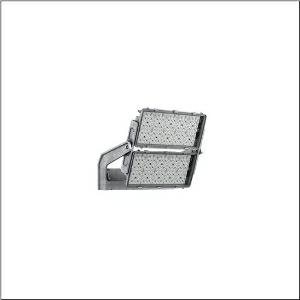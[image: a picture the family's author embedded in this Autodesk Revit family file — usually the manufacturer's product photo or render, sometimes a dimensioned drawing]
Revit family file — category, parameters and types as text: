
# Revit family: floodlight_fl_11_maxi___rs07_5xa779218k01aa_a043
name_source: partatom
category: Lighting Fixtures
units: mm (PartAtom-declared; Revit-internal decimal feet)

## family parameters
Cut with Voids When Loaded = No
Host = Face
Light Source = No
Part Type = Normal
Room Calculation Point = No
Round Connector Dimension = Use Diameter
Shared = No

## types (1)
- --- (1 x LED, 106040 lm, 941.9 W, 5700K)
    Apparent Load = 942 VA
    CIE Flux Codes = 80 93 99 100 99
    Color Rendering = 80
    Color Temperature = 5700K
    Default Elevation = 1800 mm
    Description = Floodlight FL 11  maxi floodlight; light control with lens of PMMA; cover panel of toughened safety glass, transparent; light distribution: RS07, rotationally symmetric direct distribution, LEDcolour temperature: 5700K, rated luminous flux: 106.040lm, colour rendering: CRI > 80, light colour: 857; luminous efficacy: 113lm/W; brightness control: DMX+RDM; with terminal, 6-pole, max. 2.5mm², mains connection: 220..240V/380..400V AC, 50/60Hz, surge voltage resistance: line to ground: 10kV, ECG replaceable separately, LED unit replaceable without ESD environment, dustproof LED module, dimming range 10..100%; 942W floodlight with 2x LED unit of diecast aluminium, uncoated natural; length: 713mm / width: 651mm / height: 338mm; mounting bracket, of diecast aluminium, uncoated, natural, equipment: Power, protection rating (complete): IP66; insulation class (complete): insulation class I (protective earthing); certification: CE; ball protection: ball impact resistant, only for outdoor installations, rated ambient temperature 10°C, permissible operating ambient temperature: -40..+30°C, permissible storage temperature: -40..+85°C; packaging unit: 1 piece

Light Distribution: RS07
    Height = 320 mm
    Lamp = 1 x LED
    Lamp Light Flux = 106040 lm
    Lamp Power = 941.9 W
    Lamp count = 1
    Length = 712 mm
    Luminous efficacy = 113 lm/W
    Manufacturer = Siteco
    ModVariant = No
    Model = 5XA779218K01AA
    Number of Poles = 1
    OnlyDefault = Yes
    Power Factor = 1
    Product Name = Floodlight FL 11 maxi | RS07
    Product group = floodlight | pylon top
    ProductGroupID = 6101
    Protection Class = Protection class I
    Protection Degree = IP 66
    RLX_Detail_Level = 1
    RlxData = <blob elided: 41893 chars, md5=fec89e03>
    Socket = socket
    Standby Power = 0 W
    System Light Flux = 106040 lm
    System Power = 942 W
    Type Comments = factory setting: luminous flux: 100 % | dim-lin: 254 | 975 mA
    Type Image = l_1006932.jpg
    URL = http://relux.com
    VarID = @adj_095007
    Voltage = 0 V
    Weight = 0.00 kg
    Width = 655 mm

## geometry (parser evidence)
native form markers: Blend x4, Sweep x12
no freeform markers — native parametric forms only
